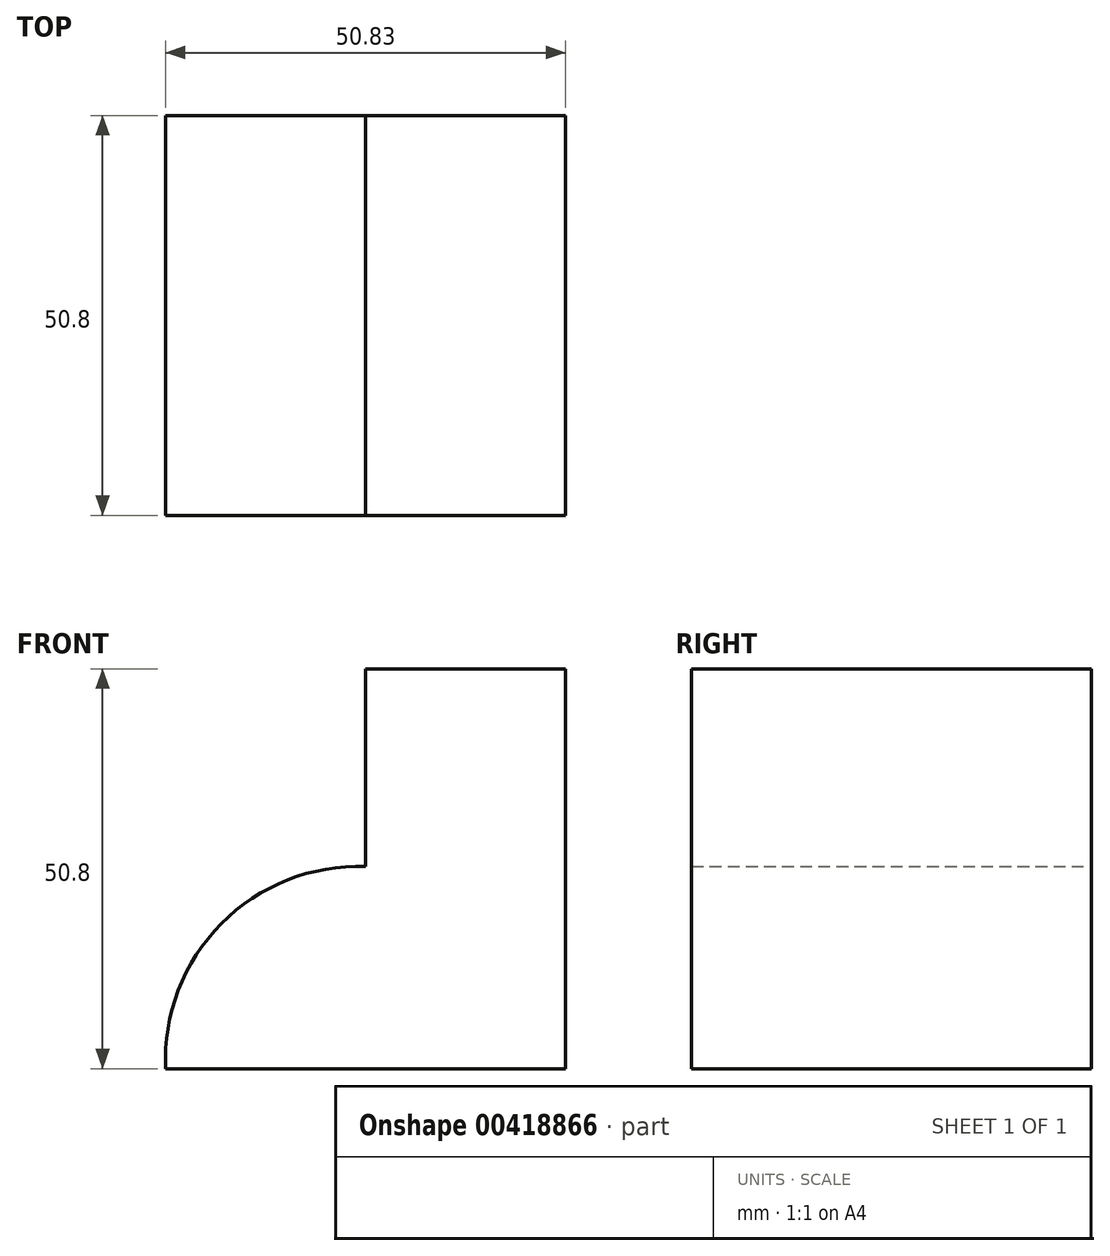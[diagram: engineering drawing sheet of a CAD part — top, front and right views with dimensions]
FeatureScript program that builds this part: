
annotation { "Feature Type Name" : "Feature", "Feature Type Description" : "" }
export const myFeature = defineFeature(function(context is Context, id is Id, definition is map)
    precondition{}
    {
        {
            var Q0;
            Q0=qCreatedBy(makeId("Front.planeOp"),FACE);
            var sketch = newSketch(context, id + "F0", { "sketchPlane" : qUnion([Q0])});
            skLineSegment(sketch, "E0", {"start": v(0, 0) * mm, "end": v(0, 50.8) * mm});
            skLineSegment(sketch, "E1", {"start": v(0, 0) * mm, "end": v(-50.8, 0) * mm});
            skLineSegment(sketch, "E2", {"start": v(0, 50.8) * mm, "end": v(-25.4, 50.8) * mm});
            skLineSegment(sketch, "E3", {"start": v(-25.4, 51.07) * mm, "end": v(-25.4, 25.67) * mm});
            skArc(sketch, "E4", {"start": v(-25.4, 25.67) * mm, "mid": v(-43.74, 18.42) * mm, "end": v(-50.8, 0) * mm});
            skSolve(sketch);
        }
        {
            var Q0;
            Q0 = qSketchRegion(id + "F0", true);
            extrude(context, id + "F1", {"entities" : qUnion([Q0]), "depth" : 50.8 * mm});
        }
    });
